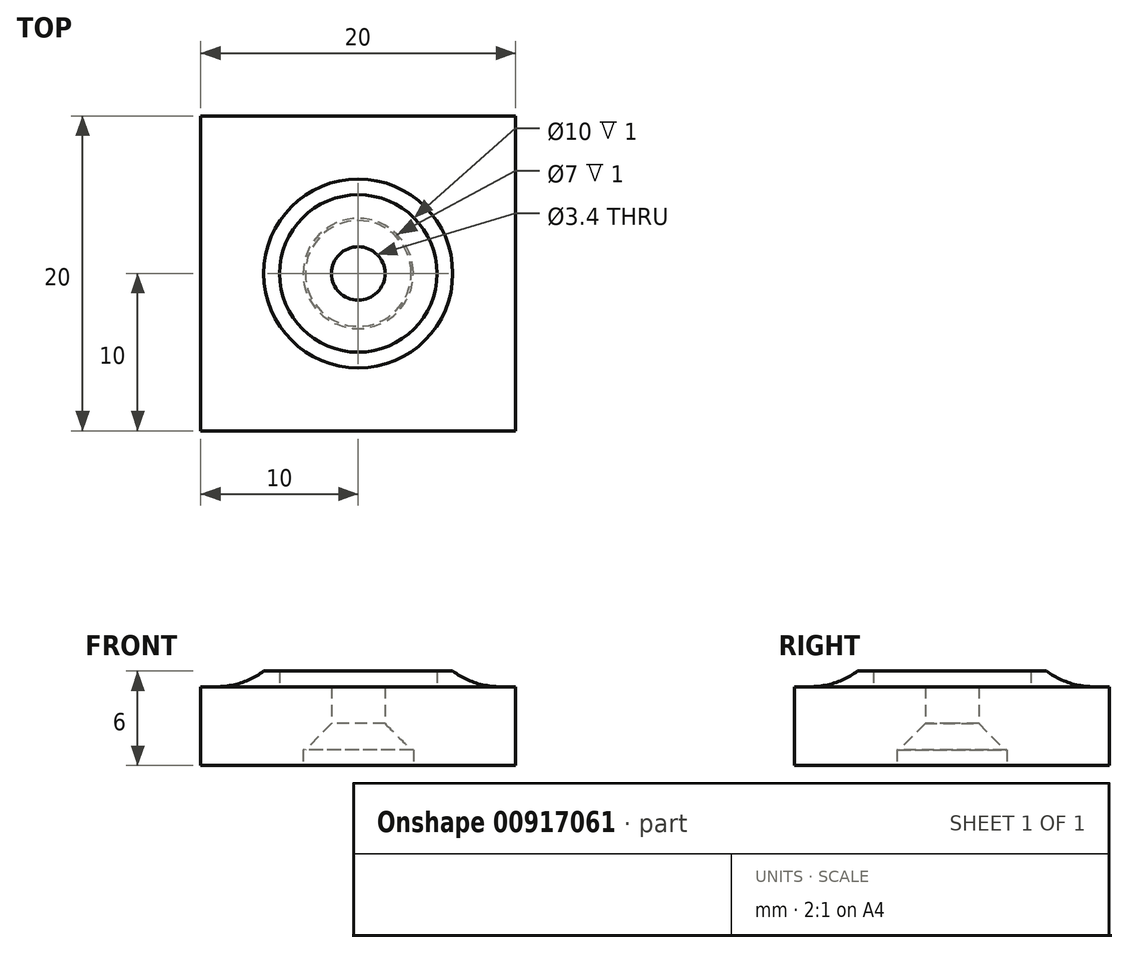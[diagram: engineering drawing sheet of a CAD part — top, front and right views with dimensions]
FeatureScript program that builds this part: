
annotation { "Feature Type Name" : "Feature", "Feature Type Description" : "" }
export const myFeature = defineFeature(function(context is Context, id is Id, definition is map)
    precondition{}
    {
        {
            var Q0;
            Q0=qCreatedBy(makeId("Top.planeOp"),FACE);
            var sketch = newSketch(context, id + "F0", { "sketchPlane" : qUnion([Q0])});
            skLineSegment(sketch, "E0.bottom", {"start": v(10, 10) * mm, "end": v(-10, 10) * mm});
            skLineSegment(sketch, "E0.top", {"start": v(10, -10) * mm, "end": v(-10, -10) * mm});
            skLineSegment(sketch, "E0.left", {"start": v(10, 10) * mm, "end": v(10, -10) * mm});
            skLineSegment(sketch, "E0.right", {"start": v(-10, 10) * mm, "end": v(-10, -10) * mm});
            skPoint(sketch, "E0.middle", {"position": v(0, 0) * mm});
            skCircle(sketch, "E1", {"center": v(0, 0) * mm, "radius": 5 * mm});
            skCircle(sketch, "E2", {"center": v(0, 0) * mm, "radius": 6 * mm});
            skCircle(sketch, "E3", {"center": v(0, 0) * mm, "radius": 3.5 * mm});
            skSolve(sketch);
        }
        {
            var Q0;
            Q0=makeQuery(id+"F0.imprint","IMPRINT",FACE,{"disambiguationData":[TD([[makeQuery(id+"F0.imprint","IMPRINT",EDGE,{"derivedFrom":sQuery(id+"F0.wireOp",EDGE,"E0.bottom")}),1.0]])]});
            var Q1;
            Q1=makeQuery(id+"F0.imprint","IMPRINT",FACE,{"disambiguationData":[TD([[makeQuery(id+"F0.imprint","IMPRINT",EDGE,{"derivedFrom":sQuery(id+"F0.wireOp",EDGE,"E1")}),-1.0]])]});
            var Q2;
            Q2=makeQuery(id+"F0.imprint","IMPRINT",FACE,{"disambiguationData":[TD([[makeQuery(id+"F0.imprint","IMPRINT",EDGE,{"derivedFrom":sQuery(id+"F0.wireOp",EDGE,"E1")}),1.0]])]});
            var Q3;
            Q3=makeQuery(id+"F0.imprint","IMPRINT",FACE,{"disambiguationData":[TD([[makeQuery(id+"F0.imprint","IMPRINT",EDGE,{"derivedFrom":sQuery(id+"F0.wireOp",EDGE,"E3")}),1.0]])]});
            extrude(context, id + "F1", {"entities" : qUnion([Q0, Q1, Q2, Q3]), "oppositeDirection" : true, "depth" : 5 * mm, "offsetDistance" : 25 * mm});
        }
        {
            var Q0;
            Q0=makeQuery(id+"F0.imprint","IMPRINT",FACE,{"disambiguationData":[TD([[makeQuery(id+"F0.imprint","IMPRINT",EDGE,{"derivedFrom":sQuery(id+"F0.wireOp",EDGE,"E1")}),-1.0]])]});
            extrude(context, id + "F2", {"entities" : qUnion([Q0]), "operationType" : NewBodyOperationType.ADD, "oppositeDirection" : true, "depth" : 6 * mm, "offsetDistance" : 25 * mm});
        }
        {
            var Q0;
            Q0=makeQuery(id+"F0.imprint","IMPRINT",FACE,{"disambiguationData":[TD([[makeQuery(id+"F0.imprint","IMPRINT",EDGE,{"derivedFrom":sQuery(id+"F0.wireOp",EDGE,"E3")}),1.0]])]});
            extrude(context, id + "F3", {"entities" : qUnion([Q0]), "operationType" : NewBodyOperationType.REMOVE, "oppositeDirection" : true, "depth" : 1 * mm, "offsetDistance" : 25 * mm});
        }
        {
            var Q0;
            Q0=sQuery(id+"F0.wireOp",VERTEX,"E0.middle");
            var Q1;
            Q1=makeQuery(id+"F1.opExtrude","SWEPT_BODY",BODY,{"disambiguationData":[OSD([sQuery(id+"F0.wireOp",EDGE,"E0.bottom"),sQuery(id+"F0.wireOp",EDGE,"E0.top"),sQuery(id+"F0.wireOp",EDGE,"E0.left"),sQuery(id+"F0.wireOp",EDGE,"E0.right")])]});
            hole(context, id + "F4", {"style" : HoleStyle.C_SINK, "endStyle" : HoleEndStyle.THROUGH, "standardTappedOrClearance" : lookupTablePath({ "fit" : "Normal", "standard" : "ISO", "size" : "M3", "type" : "Clearance" }), "standardBlindInLast" : lookupTablePath({ "fit" : "Normal", "standard" : "ISO", "size" : "M3", "type" : "Clearance" }), "holeDiameter" : 3.4 * mm, "cSinkDiameter" : 6.72 * mm, "cSinkAngle" : 90 * degree, "majorDiameter" : 5 * mm, "isTappedThrough" : true, "tappedDepth" : 12 * mm, "tapClearance" : 3, "locations" : qUnion([Q0]), "scope" : qUnion([Q1])});
        }
        {
            var Q0;
            Q0=makeQuery(id+"F2.boolean.opBoolean","INTERSECT",EDGE,{"derivedFrom":[makeQuery(id+"F1.opExtrude","CAP_FACE",FACE,{"disambiguationData":[OSD([sQuery(id+"F0.wireOp",EDGE,"E0.bottom"),sQuery(id+"F0.wireOp",EDGE,"E0.top"),sQuery(id+"F0.wireOp",EDGE,"E0.left"),sQuery(id+"F0.wireOp",EDGE,"E0.right")])],"isStart":false}),makeQuery(id+"F2.opExtrude","SWEPT_FACE",FACE,{"disambiguationData":[OSD([sQuery(id+"F0.wireOp",EDGE,"E2")])]})]});
            fillet(context, id + "F5", {"entities" : qUnion([Q0]), "radius" : 5 * mm, "tangentPropagation" : true, "allowEdgeOverflow" : false});
        }
        {
            var Q0;
            Q0=makeQuery(id+"F1.opExtrude","SWEPT_BODY",BODY,{"disambiguationData":[OSD([sQuery(id+"F0.wireOp",EDGE,"E0.bottom"),sQuery(id+"F0.wireOp",EDGE,"E0.top"),sQuery(id+"F0.wireOp",EDGE,"E0.left"),sQuery(id+"F0.wireOp",EDGE,"E0.right")])]});
            var Q1;
            Q1=makeQuery(id+"F1.opExtrude","CAP_EDGE",EDGE,{"disambiguationData":[OSD([sQuery(id+"F0.wireOp",EDGE,"E0.bottom")])],"isStart":true});
            transform(context, id + "F6", {"entities" : qUnion([Q0]), "transformType" : TransformType.ROTATION, "transformAxis" : qUnion([Q1]), "angle" : 180 * degree, "makeCopy" : false});
        }
    });
